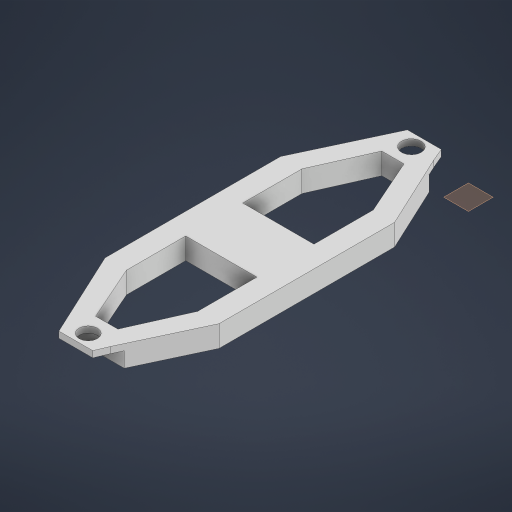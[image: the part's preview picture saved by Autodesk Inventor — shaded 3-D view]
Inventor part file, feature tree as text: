
AUTODESK INVENTOR PART (.ipt)
format: ipt  version: 2023 (Build 270158000, 158)  size: 272,896 bytes
history: native  units: in
note: dims shown in document units (in); Inventor stores cm internally (conversion verified against a paired STEP export)
features: extrude x5, sketch x4, plane x1
ambient origin geometry x8: Origin, YZ Plane, XZ Plane, XY Plane, X Axis, Y Axis, Z Axis, Center Point
bodies: Solid1 (feature_tree)
feature tree (10):
  extrude  "Extrusion1"  Depth=0.75in TaperAngle=0.0deg
  extrude  "Extrusion9"  Depth=0.75in
  extrude  "Extrusion10"  Depth=4.0in
  plane  "Work Plane1"
  extrude  "Extrusion13"  Depth=0.75in
  extrude  "Extrusion14"  Depth=0.75in
  sketch  "Sketch1"  dims[d3=0.75in d8=0.75in d9=0.0in]
  sketch  "Sketch9"  dims[d49=11.0236in d50=0.75in]
  sketch  "Sketch10"  dims[d51=0.7902in d52=4.0in]
  sketch  "Sketch13"  dims[d53=2.0in d55=0.3125in d56=0.445in d57=180.0deg d58=0.75in d59=0.0in d60=0.75in d61=0.0in d68=0.645in d69=0.69in d70=11.3386in d71=11.3386in d72=1.0in d73=0.0in d74=0.0in d75=0.0in]
